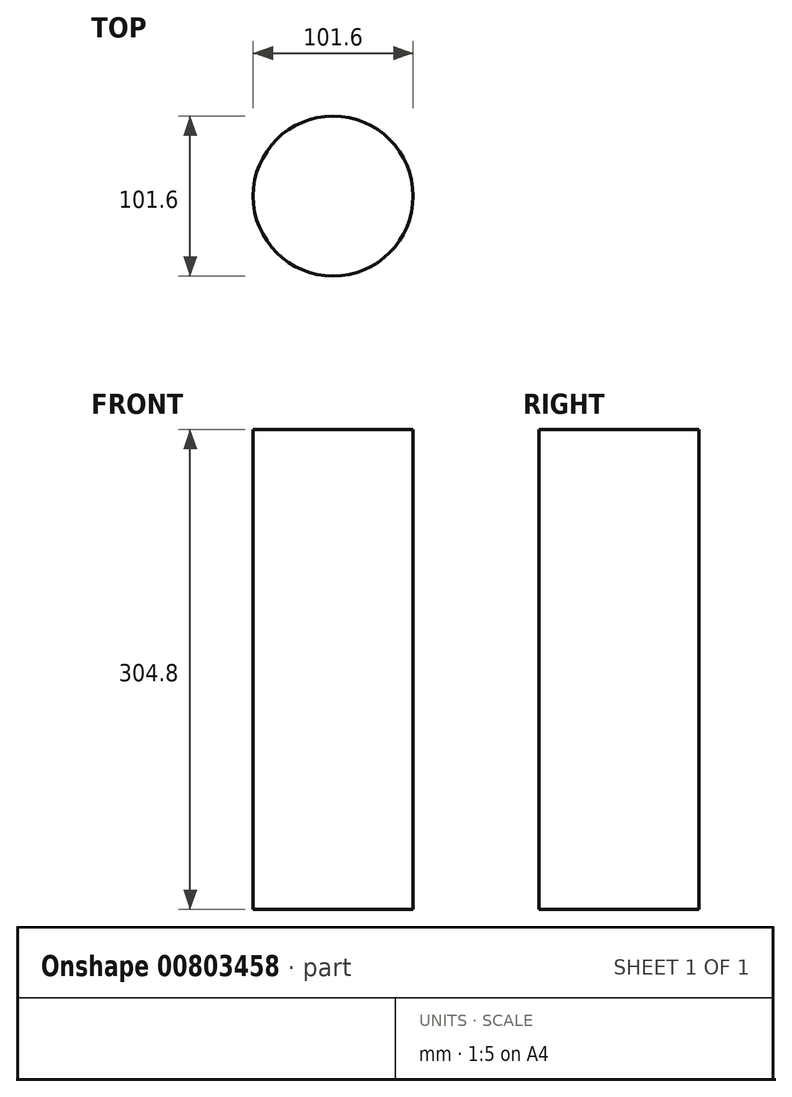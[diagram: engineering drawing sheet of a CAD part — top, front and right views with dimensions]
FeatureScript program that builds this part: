
annotation { "Feature Type Name" : "Feature", "Feature Type Description" : "" }
export const myFeature = defineFeature(function(context is Context, id is Id, definition is map)
    precondition{}
    {
        {
            var Q0;
            Q0=qCreatedBy(makeId("Top.planeOp"),FACE);
            var sketch = newSketch(context, id + "F0", { "sketchPlane" : qUnion([Q0])});
            skCircle(sketch, "E0", {"center": v(0, 0) * mm, "radius": 50.8 * mm});
            skSolve(sketch);
        }
        {
            var Q0;
            Q0=makeQuery(id+"F0.imprint","IMPRINT",FACE,{"disambiguationData":[TD([[makeQuery(id+"F0.imprint","IMPRINT",EDGE,{"derivedFrom":sQuery(id+"F0.wireOp",EDGE,"E0")}),1.0]])]});
            extrude(context, id + "F1", {"entities" : qUnion([Q0]), "endBound" : BoundingType.SYMMETRIC, "depth" : 304.8 * mm, "offsetDistance" : 25.4 * mm});
        }
    });
